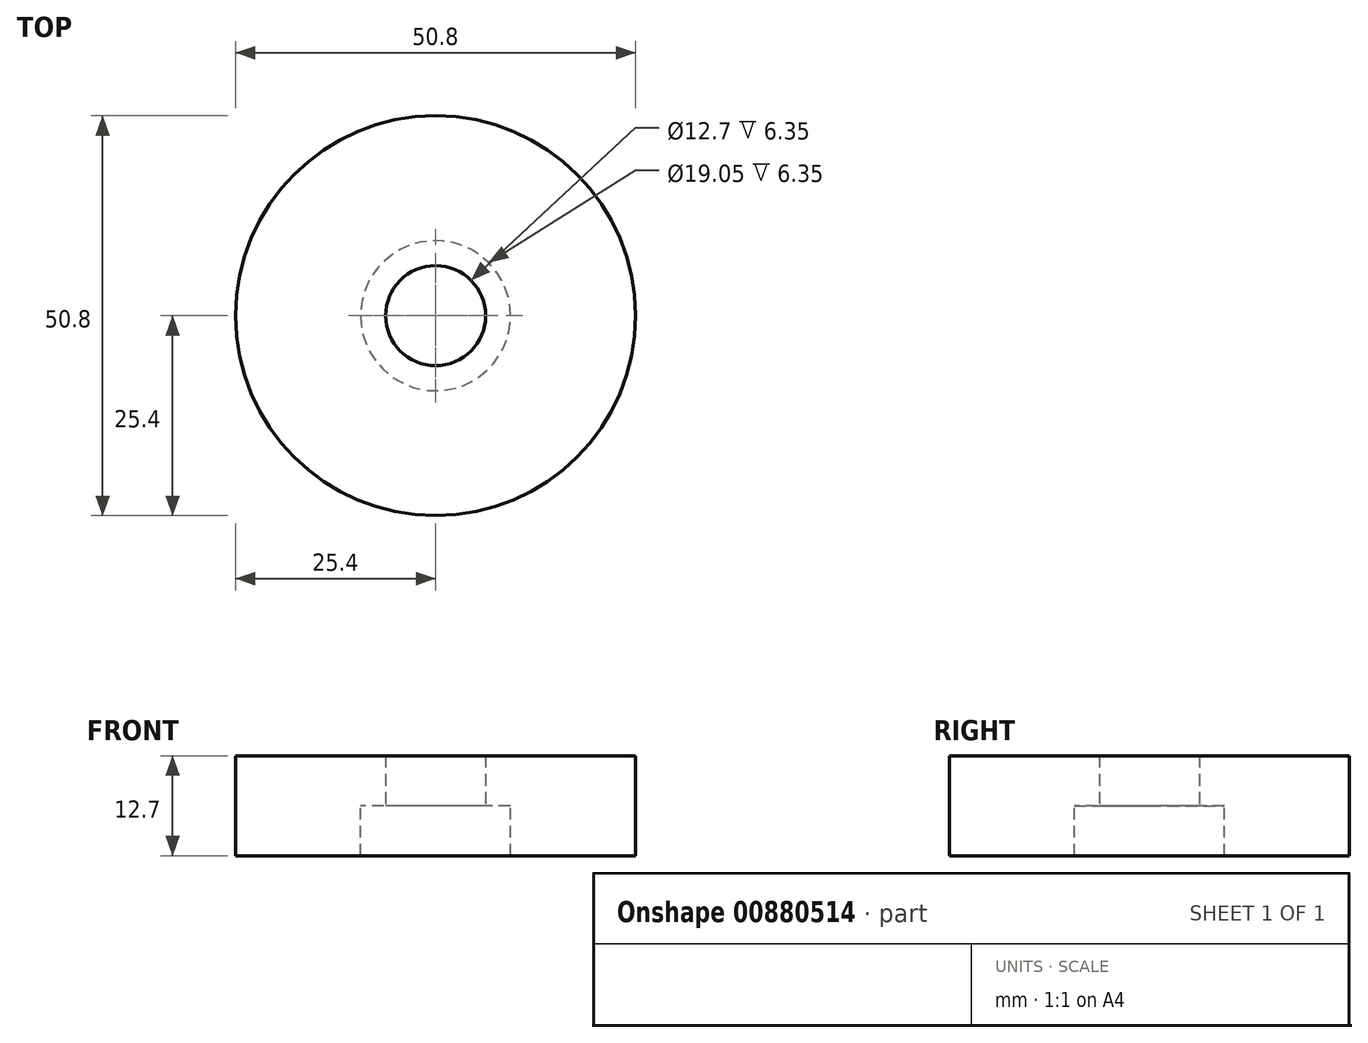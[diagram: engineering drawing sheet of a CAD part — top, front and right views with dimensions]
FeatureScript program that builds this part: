
annotation { "Feature Type Name" : "Feature", "Feature Type Description" : "" }
export const myFeature = defineFeature(function(context is Context, id is Id, definition is map)
    precondition{}
    {
        {
            var Q0;
            Q0=qCreatedBy(makeId("Top.planeOp"),FACE);
            var sketch = newSketch(context, id + "F0", { "sketchPlane" : qUnion([Q0])});
            skCircle(sketch, "E0", {"center": v(0, 0) * mm, "radius": 25.4 * mm});
            skCircle(sketch, "E1", {"center": v(0, 0) * mm, "radius": 6.35 * mm});
            skSolve(sketch);
        }
        {
            var Q0;
            Q0 = qSketchRegion(id + "F0", true);
            extrude(context, id + "F1", {"entities" : qUnion([Q0]), "endBound" : BoundingType.SYMMETRIC, "depth" : 12.7 * mm, "offsetDistance" : 25.4 * mm});
        }
        {
            var Q0;
            Q0=qCreatedBy(makeId("Top.planeOp"),FACE);
            var sketch = newSketch(context, id + "F2", { "sketchPlane" : qUnion([Q0])});
            skCircle(sketch, "E2", {"center": v(0, 0) * mm, "radius": 9.53 * mm});
            skSolve(sketch);
        }
        {
            var Q0;
            Q0 = qSketchRegion(id + "F2", true);
            extrude(context, id + "F3", {"entities" : qUnion([Q0]), "operationType" : NewBodyOperationType.REMOVE, "oppositeDirection" : true, "depth" : 6.35 * mm, "offsetDistance" : 25.4 * mm});
        }
    });
